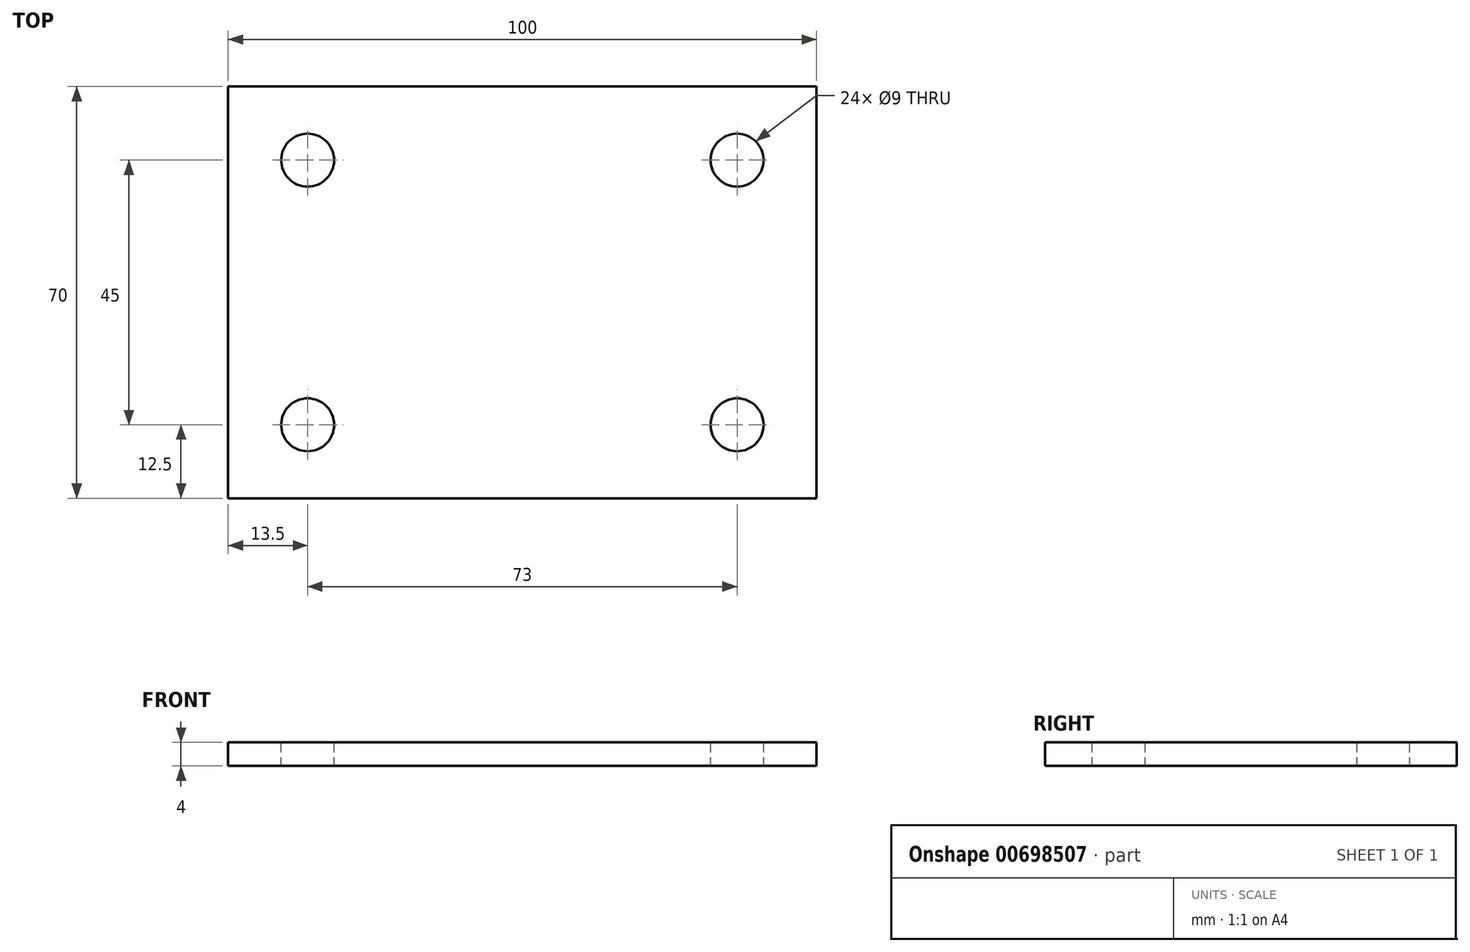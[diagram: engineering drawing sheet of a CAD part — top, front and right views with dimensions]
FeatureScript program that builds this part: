
annotation { "Feature Type Name" : "Feature", "Feature Type Description" : "" }
export const myFeature = defineFeature(function(context is Context, id is Id, definition is map)
    precondition{}
    {
        {
            var Q0;
            Q0=qCreatedBy(makeId("Top.planeOp"),FACE);
            var sketch = newSketch(context, id + "F0", { "sketchPlane" : qUnion([Q0])});
            skLineSegment(sketch, "E0.bottom", {"start": v(-50, 35) * mm, "end": v(50, 35) * mm});
            skLineSegment(sketch, "E0.top", {"start": v(-50, -35) * mm, "end": v(50, -35) * mm});
            skLineSegment(sketch, "E0.left", {"start": v(-50, 35) * mm, "end": v(-50, -35) * mm});
            skLineSegment(sketch, "E0.right", {"start": v(50, 35) * mm, "end": v(50, -35) * mm});
            skSolve(sketch);
        }
        {
            var Q0;
            Q0 = qSketchRegion(id + "F0", true);
            extrude(context, id + "F1", {"entities" : qUnion([Q0]), "oppositeDirection" : true, "depth" : 4 * mm, "offsetDistance" : 25 * mm});
        }
        {
            var Q0;
            Q0=makeQuery(id+"F1.opExtrude","CAP_FACE",FACE,{"disambiguationData":[OSD([sQuery(id+"F0.wireOp",EDGE,"E0.bottom"),sQuery(id+"F0.wireOp",EDGE,"E0.top"),sQuery(id+"F0.wireOp",EDGE,"E0.left"),sQuery(id+"F0.wireOp",EDGE,"E0.right")])],"isStart":true});
            var sketch = newSketch(context, id + "F2", { "sketchPlane" : qUnion([Q0])});
            skCircle(sketch, "E1", {"center": v(-36.5, 22.5) * mm, "radius": 4.5 * mm});
            skCircle(sketch, "E2.MirrorC", {"center": v(36.5, 22.5) * mm, "radius": 4.5 * mm});
            skCircle(sketch, "E3.MirrorC", {"center": v(-36.5, -22.5) * mm, "radius": 4.5 * mm});
            skCircle(sketch, "E4.MirrorC", {"center": v(36.5, -22.5) * mm, "radius": 4.5 * mm});
            skSolve(sketch);
        }
        {
            var Q0;
            Q0 = qSketchRegion(id + "F2", true);
            extrude(context, id + "F3", {"entities" : qUnion([Q0]), "operationType" : NewBodyOperationType.REMOVE, "endBound" : BoundingType.UP_TO_NEXT, "oppositeDirection" : true, "depth" : 25 * mm, "offsetDistance" : 25 * mm});
        }
    });
